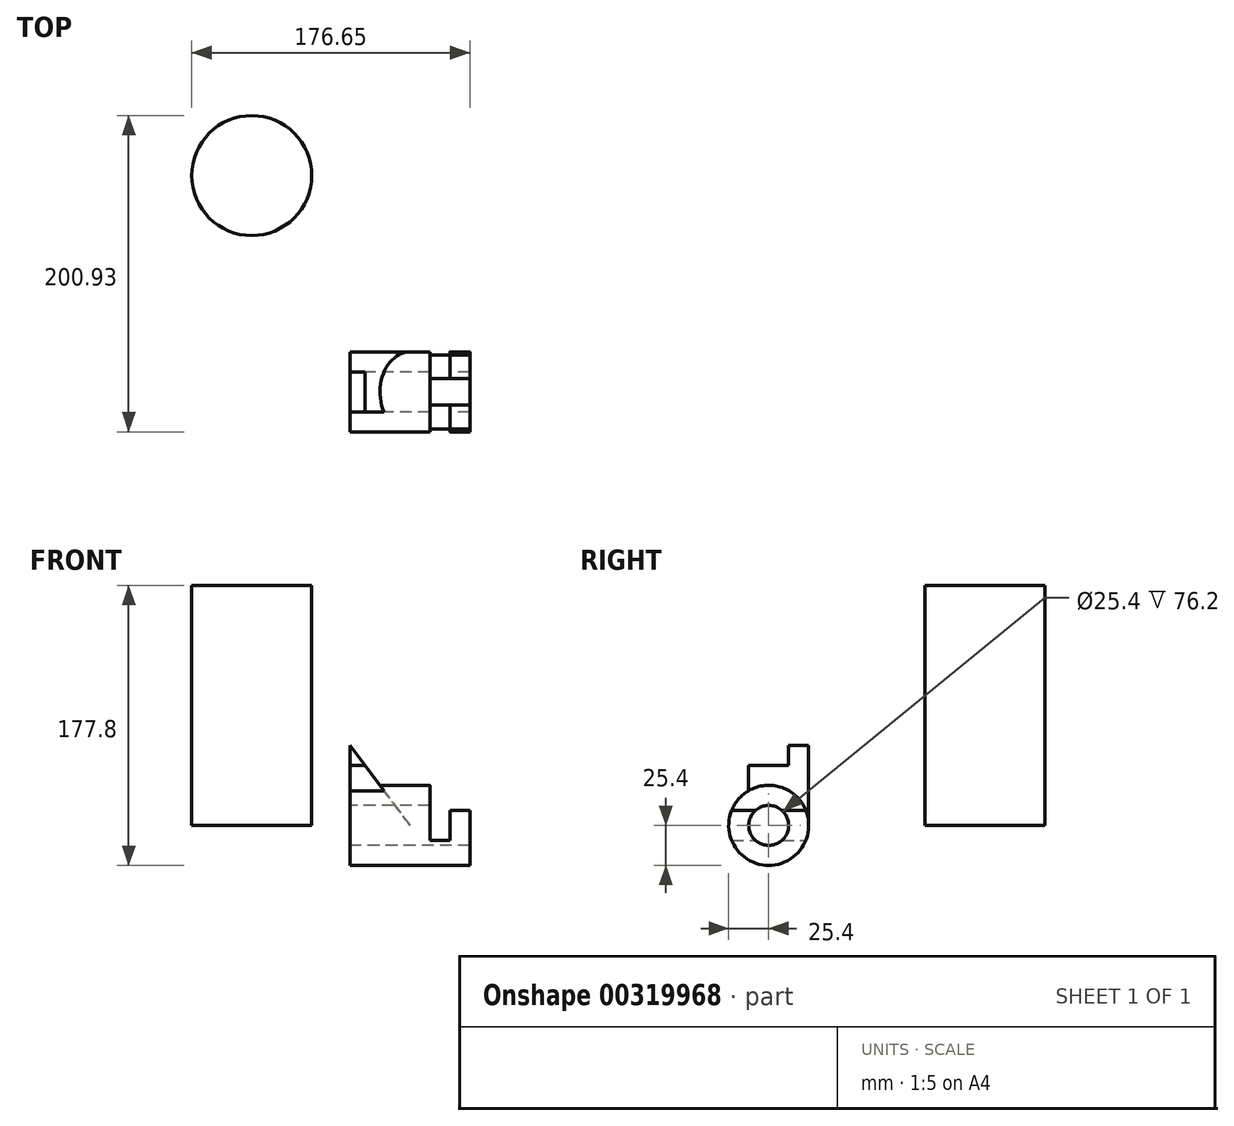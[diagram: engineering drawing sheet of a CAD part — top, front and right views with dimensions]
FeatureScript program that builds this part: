
annotation { "Feature Type Name" : "Feature", "Feature Type Description" : "" }
export const myFeature = defineFeature(function(context is Context, id is Id, definition is map)
    precondition{}
    {
        {
            var Q0;
            Q0=qCreatedBy(makeId("Right.planeOp"),FACE);
            var sketch = newSketch(context, id + "F0", { "sketchPlane" : qUnion([Q0])});
            skCircle(sketch, "E0", {"center": v(0, 0) * mm, "radius": 12.7 * mm});
            skCircle(sketch, "E1", {"center": v(0, 0) * mm, "radius": 25.4 * mm});
            skSolve(sketch);
        }
        {
            var Q0;
            Q0 = qSketchRegion(id + "F0", true);
            extrude(context, id + "F1", {"entities" : qUnion([Q0]), "depth" : 50.8 * mm});
        }
        {
            var Q0;
            Q0=makeQuery(id+"F1.opExtrude","CAP_FACE",FACE,{"disambiguationData":[OSD([sQuery(id+"F0.wireOp",EDGE,"E0"),sQuery(id+"F0.wireOp",EDGE,"E1")])],"isStart":false});
            var sketch = newSketch(context, id + "F2", { "sketchPlane" : qUnion([Q0])});
            skLineSegment(sketch, "E2", {"start": v(-23.55, 9.53) * mm, "end": v(23.55, 9.53) * mm});
            skLineSegment(sketch, "E3", {"start": v(-23.55, -9.53) * mm, "end": v(23.55, -9.53) * mm});
            skSolve(sketch);
        }
        {
            var Q0;
            {var subQ0=sQuery(id+"F2.wireOp",EDGE,"E3");var subQ1=makeQuery(id+"F1.opExtrude","CAP_EDGE",EDGE,{"disambiguationData":[OSD([sQuery(id+"F0.wireOp",EDGE,"E1")])],"isStart":false});var subQ2=makeQuery(id+"F2.imprint","INTERSECT",VERTEX,{"disambiguationData":[OD(0.0)],"derivedFrom":[subQ1,subQ0]});Q0=makeQuery(id+"F2.imprint","IMPRINT",FACE,{"disambiguationData":[TD([[makeQuery(id+"F2.imprint","IMPRINT",EDGE,{"disambiguationData":[TD([[subQ2,-1.0]])],"derivedFrom":subQ0}),-1.0]])]});}
            extrude(context, id + "F3", {"entities" : qUnion([Q0]), "operationType" : NewBodyOperationType.ADD, "depth" : 12.7 * mm});
        }
        {
            var Q0;
            Q0=makeQuery(id+"F3.opExtrude","CAP_FACE",FACE,{"disambiguationData":[OSD([sQuery(id+"F0.wireOp",EDGE,"E0"),sQuery(id+"F0.wireOp",EDGE,"E1"),sQuery(id+"F2.wireOp",EDGE,"E3")])],"isStart":false});
            var sketch = newSketch(context, id + "F4", { "sketchPlane" : qUnion([Q0])});
            skLineSegment(sketch, "E4.0", {"start": v(-23.55, 9.53) * mm, "end": v(23.55, 9.53) * mm});
            skArc(sketch, "E5.0", {"start": v(-23.55, -9.52) * mm, "mid": v(0, -25.4) * mm, "end": v(23.55, -9.52) * mm});
            skArc(sketch, "E6.0", {"start": v(23.55, -9.52) * mm, "mid": v(0, 25.4) * mm, "end": v(-23.55, -9.52) * mm});
            skArc(sketch, "E7.0", {"start": v(8.4, -9.53) * mm, "mid": v(0, 12.7) * mm, "end": v(-8.4, -9.52) * mm});
            skArc(sketch, "E8.0", {"start": v(-8.4, -9.52) * mm, "mid": v(0, -12.7) * mm, "end": v(8.4, -9.53) * mm});
            skSolve(sketch);
        }
        {
            var Q0;
            {var subQ5=sQuery(id+"F2.wireOp",EDGE,"E3");var subQ6=makeQuery(id+"F3.opExtrude","CAP_EDGE",EDGE,{"disambiguationData":[OSD([subQ5]),TDD([makeQuery(id+"F2.imprint","IMPRINT",EDGE,{"disambiguationData":[TD([[makeQuery(id+"F2.imprint","INTERSECT",VERTEX,{"disambiguationData":[OD(0.0)],"derivedFrom":[makeQuery(id+"F1.opExtrude","CAP_EDGE",EDGE,{"disambiguationData":[OSD([sQuery(id+"F0.wireOp",EDGE,"E1")])],"isStart":false}),subQ5]}),-1.0]])],"derivedFrom":subQ5})])],"isStart":false});Q0=makeQuery(id+"F4.imprint","IMPRINT",FACE,{"disambiguationData":[TD([[makeQuery(id+"F4.imprint","IMPRINT",EDGE,{"derivedFrom":subQ6}),1.0]])]});}
            var Q1;
            {var subQ5=sQuery(id+"F2.wireOp",EDGE,"E3");var subQ6=makeQuery(id+"F3.opExtrude","CAP_EDGE",EDGE,{"disambiguationData":[OSD([subQ5]),TDD([makeQuery(id+"F2.imprint","IMPRINT",EDGE,{"disambiguationData":[TD([[makeQuery(id+"F2.imprint","INTERSECT",VERTEX,{"disambiguationData":[OD(1.0)],"derivedFrom":[makeQuery(id+"F1.opExtrude","CAP_EDGE",EDGE,{"disambiguationData":[OSD([sQuery(id+"F0.wireOp",EDGE,"E1")])],"isStart":false}),subQ5]}),1.0]])],"derivedFrom":subQ5})])],"isStart":false});Q1=makeQuery(id+"F4.imprint","IMPRINT",FACE,{"disambiguationData":[TD([[makeQuery(id+"F4.imprint","IMPRINT",EDGE,{"derivedFrom":subQ6}),1.0]])]});}
            var Q2;
            Q2=makeQuery(id+"F4.imprint","IMPRINT",FACE,{"disambiguationData":[TD([[makeQuery(id+"F4.imprint","IMPRINT",EDGE,{"derivedFrom":sQuery(id+"F4.wireOp",EDGE,"E5.0")}),1.0]])]});
            extrude(context, id + "F5", {"entities" : qUnion([Q0, Q1, Q2]), "operationType" : NewBodyOperationType.ADD, "depth" : 12.7 * mm});
        }
        {
            var Q0;
            Q0=qCreatedBy(makeId("Front.planeOp"),FACE);
            cPlane(context, id + "F6", {"entities" : qUnion([Q0]), "cplaneType" : CPlaneType.OFFSET, "offset" : 25.4 * mm, "oppositeDirection" : true, "width" : 152.4 * mm, "height" : 152.4 * mm});
        }
        {
            var Q0;
            Q0=qCreatedBy(id+"F6.planeOp",FACE);
            var sketch = newSketch(context, id + "F7", { "sketchPlane" : qUnion([Q0])});
            skLineSegment(sketch, "E9", {"start": v(0, 0) * mm, "end": v(0, 50.8) * mm});
            skLineSegment(sketch, "E10", {"start": v(38.1, 0) * mm, "end": v(0, 0) * mm});
            skLineSegment(sketch, "E11", {"start": v(0, 50.8) * mm, "end": v(38.1, 0) * mm});
            skSolve(sketch);
        }
        {
            var Q0;
            Q0 = qSketchRegion(id + "F7", true);
            extrude(context, id + "F8", {"entities" : qUnion([Q0]), "operationType" : NewBodyOperationType.ADD, "depth" : 38.1 * mm});
        }
        {
            var Q0;
            {var subQ0=sQuery(id+"F2.wireOp",EDGE,"E2");var subQ1=makeQuery(id+"F1.opExtrude","CAP_EDGE",EDGE,{"disambiguationData":[OSD([sQuery(id+"F0.wireOp",EDGE,"E0")])],"isStart":false});var subQ2=makeQuery(id+"F2.imprint","INTERSECT",VERTEX,{"disambiguationData":[OD(0.0)],"derivedFrom":[subQ1,subQ0]});Q0=makeQuery(id+"F2.imprint","IMPRINT",FACE,{"disambiguationData":[TD([[makeQuery(id+"F2.imprint","IMPRINT",EDGE,{"disambiguationData":[TD([[subQ2,-1.0]])],"derivedFrom":subQ0}),1.0]])]});}
            var Q1;
            {var subQ0=sQuery(id+"F2.wireOp",EDGE,"E2");var subQ1=makeQuery(id+"F1.opExtrude","CAP_EDGE",EDGE,{"disambiguationData":[OSD([sQuery(id+"F0.wireOp",EDGE,"E0")])],"isStart":false});var subQ2=makeQuery(id+"F2.imprint","INTERSECT",VERTEX,{"disambiguationData":[OD(0.0)],"derivedFrom":[subQ1,subQ0]});Q1=makeQuery(id+"F2.imprint","IMPRINT",FACE,{"disambiguationData":[TD([[makeQuery(id+"F2.imprint","IMPRINT",EDGE,{"disambiguationData":[TD([[subQ2,-1.0]])],"derivedFrom":subQ0}),-1.0]])]});}
            extrude(context, id + "F9", {"entities" : qUnion([Q0, Q1]), "operationType" : NewBodyOperationType.REMOVE, "endBound" : BoundingType.THROUGH_ALL, "oppositeDirection" : true, "depth" : 25.4 * mm});
        }
        {
            var Q0;
            Q0=makeQuery(id+"F8.boolean.opBoolean","MERGE",FACE,{"derivedFrom":[makeQuery(id+"F1.opExtrude","CAP_FACE",FACE,{"disambiguationData":[OSD([sQuery(id+"F0.wireOp",EDGE,"E0"),sQuery(id+"F0.wireOp",EDGE,"E1")])],"isStart":true}),makeQuery(id+"F8.opExtrude","SWEPT_FACE",FACE,{"disambiguationData":[OSD([sQuery(id+"F7.wireOp",EDGE,"E9")])]})]});
            var sketch = newSketch(context, id + "F10", { "sketchPlane" : qUnion([Q0])});
            skLineSegment(sketch, "E12", {"start": v(-12.7, 50.8) * mm, "end": v(-12.7, 38.1) * mm});
            skLineSegment(sketch, "E13", {"start": v(-12.7, 38.1) * mm, "end": v(12.7, 38.1) * mm});
            skLineSegment(sketch, "E14", {"start": v(12.7, 38.1) * mm, "end": v(12.7, 50.8) * mm});
            skLineSegment(sketch, "E15", {"start": v(12.7, 50.8) * mm, "end": v(-12.7, 50.8) * mm});
            skSolve(sketch);
        }
        {
            var Q0;
            Q0 = qSketchRegion(id + "F10", true);
            extrude(context, id + "F11", {"entities" : qUnion([Q0]), "operationType" : NewBodyOperationType.REMOVE, "oppositeDirection" : true, "depth" : 25.4 * mm});
        }
        {
            var Q0;
            Q0=qCreatedBy(makeId("Top.planeOp"),FACE);
            var sketch = newSketch(context, id + "F12", { "sketchPlane" : qUnion([Q0])});
            skCircle(sketch, "E16", {"center": v(-62.35, 137.43) * mm, "radius": 38.1 * mm});
            skSolve(sketch);
        }
        {
            var Q0;
            Q0=makeQuery(id+"F12.imprint","IMPRINT",FACE,{"disambiguationData":[TD([[makeQuery(id+"F12.imprint","IMPRINT",EDGE,{"derivedFrom":sQuery(id+"F12.wireOp",EDGE,"E16")}),1.0]])]});
            extrude(context, id + "F13", {"entities" : qUnion([Q0]), "depth" : 152.4 * mm, "offsetDistance" : 25.4 * mm});
        }
    });
